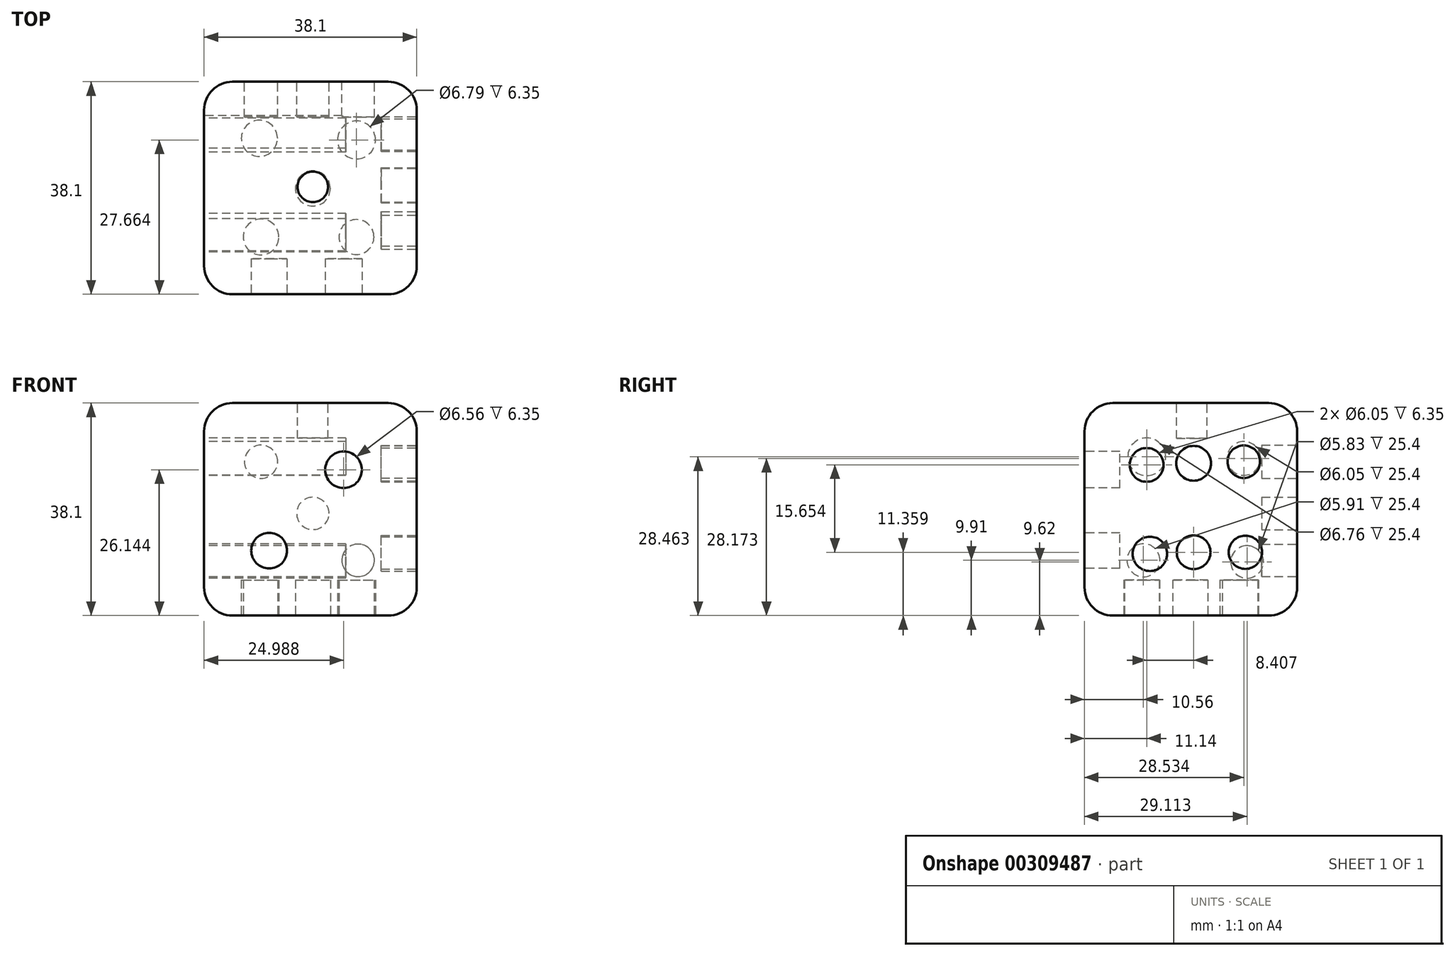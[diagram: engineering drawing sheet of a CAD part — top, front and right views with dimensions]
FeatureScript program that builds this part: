
annotation { "Feature Type Name" : "Feature", "Feature Type Description" : "" }
export const myFeature = defineFeature(function(context is Context, id is Id, definition is map)
    precondition{}
    {
        {
            var Q0;
            Q0=qCreatedBy(makeId("Front.planeOp"),FACE);
            var sketch = newSketch(context, id + "F0", { "sketchPlane" : qUnion([Q0])});
            skLineSegment(sketch, "E0.bottom", {"start": v(-19.48, 2.68) * mm, "end": v(18.62, 2.68) * mm});
            skLineSegment(sketch, "E0.top", {"start": v(-19.48, -35.42) * mm, "end": v(18.62, -35.42) * mm});
            skLineSegment(sketch, "E0.left", {"start": v(-19.48, 2.68) * mm, "end": v(-19.48, -35.42) * mm});
            skLineSegment(sketch, "E0.right", {"start": v(18.62, 2.68) * mm, "end": v(18.62, -35.42) * mm});
            skSolve(sketch);
        }
        {
            var Q0;
            Q0=makeQuery(id+"F0.imprint","IMPRINT",FACE,{"disambiguationData":[TD([[makeQuery(id+"F0.imprint","IMPRINT",EDGE,{"derivedFrom":sQuery(id+"F0.wireOp",EDGE,"E0.bottom")}),-1.0]])]});
            extrude(context, id + "F1", {"entities" : qUnion([Q0]), "depth" : 38.1 * mm});
        }
        {
            var Q0;
            Q0=makeQuery(id+"F1.opExtrude","SWEPT_EDGE",EDGE,{"disambiguationData":[OSD([sQuery(id+"F0.wireOp",EDGE,"E0.bottom"),sQuery(id+"F0.wireOp",EDGE,"E0.left")])]});
            var Q1;
            Q1=makeQuery(id+"F1.opExtrude","CAP_EDGE",EDGE,{"disambiguationData":[OSD([sQuery(id+"F0.wireOp",EDGE,"E0.bottom")])],"isStart":false});
            var Q2;
            Q2=makeQuery(id+"F1.opExtrude","SWEPT_EDGE",EDGE,{"disambiguationData":[OSD([sQuery(id+"F0.wireOp",EDGE,"E0.bottom"),sQuery(id+"F0.wireOp",EDGE,"E0.right")])]});
            var Q3;
            Q3=makeQuery(id+"F1.opExtrude","CAP_EDGE",EDGE,{"disambiguationData":[OSD([sQuery(id+"F0.wireOp",EDGE,"E0.bottom")])],"isStart":true});
            var Q4;
            Q4=makeQuery(id+"F1.opExtrude","CAP_EDGE",EDGE,{"disambiguationData":[OSD([sQuery(id+"F0.wireOp",EDGE,"E0.right")])],"isStart":true});
            var Q5;
            Q5=makeQuery(id+"F1.opExtrude","SWEPT_EDGE",EDGE,{"disambiguationData":[OSD([sQuery(id+"F0.wireOp",EDGE,"E0.top"),sQuery(id+"F0.wireOp",EDGE,"E0.right")])]});
            var Q6;
            Q6=makeQuery(id+"F1.opExtrude","CAP_EDGE",EDGE,{"disambiguationData":[OSD([sQuery(id+"F0.wireOp",EDGE,"E0.top")])],"isStart":true});
            var Q7;
            Q7=makeQuery(id+"F1.opExtrude","CAP_EDGE",EDGE,{"disambiguationData":[OSD([sQuery(id+"F0.wireOp",EDGE,"E0.right")])],"isStart":false});
            var Q8;
            Q8=makeQuery(id+"F1.opExtrude","CAP_EDGE",EDGE,{"disambiguationData":[OSD([sQuery(id+"F0.wireOp",EDGE,"E0.left")])],"isStart":false});
            var Q9;
            Q9=makeQuery(id+"F1.opExtrude","CAP_EDGE",EDGE,{"disambiguationData":[OSD([sQuery(id+"F0.wireOp",EDGE,"E0.top")])],"isStart":false});
            var Q10;
            Q10=makeQuery(id+"F1.opExtrude","SWEPT_EDGE",EDGE,{"disambiguationData":[OSD([sQuery(id+"F0.wireOp",EDGE,"E0.top"),sQuery(id+"F0.wireOp",EDGE,"E0.left")])]});
            var Q11;
            Q11=makeQuery(id+"F1.opExtrude","SWEPT_FACE",FACE,{"disambiguationData":[OSD([sQuery(id+"F0.wireOp",EDGE,"E0.left")])]});
            fillet(context, id + "F2", {"entities" : qUnion([Q0, Q1, Q2, Q3, Q4, Q5, Q6, Q7, Q8, Q9, Q10, Q11]), "radius" : 5.08 * mm, "tangentPropagation" : true, "allowEdgeOverflow" : false});
        }
        {
            var Q0;
            Q0=makeQuery(id+"F1.opExtrude","SWEPT_FACE",FACE,{"disambiguationData":[OSD([sQuery(id+"F0.wireOp",EDGE,"E0.bottom")])]});
            var sketch = newSketch(context, id + "F3", { "sketchPlane" : qUnion([Q0])});
            skCircle(sketch, "E1", {"center": v(0, -18.84) * mm, "radius": 2.73 * mm});
            skSolve(sketch);
        }
        {
            var Q0;
            Q0 = qSketchRegion(id + "F3", true);
            extrude(context, id + "F4", {"entities" : qUnion([Q0]), "operationType" : NewBodyOperationType.REMOVE, "oppositeDirection" : true, "depth" : 6.35 * mm});
        }
        {
            var Q0;
            Q0=makeQuery(id+"F1.opExtrude","CAP_FACE",FACE,{"disambiguationData":[OSD([sQuery(id+"F0.wireOp",EDGE,"E0.bottom"),sQuery(id+"F0.wireOp",EDGE,"E0.top"),sQuery(id+"F0.wireOp",EDGE,"E0.left"),sQuery(id+"F0.wireOp",EDGE,"E0.right")])],"isStart":false});
            var sketch = newSketch(context, id + "F5", { "sketchPlane" : qUnion([Q0])});
            skCircle(sketch, "E2", {"center": v(-7.83, -23.77) * mm, "radius": 3.2 * mm});
            skCircle(sketch, "E3", {"center": v(5.5, -9.28) * mm, "radius": 3.28 * mm});
            skSolve(sketch);
        }
        {
            var Q0;
            Q0 = qSketchRegion(id + "F5", true);
            extrude(context, id + "F6", {"entities" : qUnion([Q0]), "operationType" : NewBodyOperationType.REMOVE, "oppositeDirection" : true, "depth" : 6.35 * mm});
        }
        {
            var Q0;
            Q0=makeQuery(id+"F1.opExtrude","SWEPT_FACE",FACE,{"disambiguationData":[OSD([sQuery(id+"F0.wireOp",EDGE,"E0.top")])]});
            var sketch = newSketch(context, id + "F7", { "sketchPlane" : qUnion([Q0])});
            skCircle(sketch, "E4", {"center": v(0, 19.13) * mm, "radius": 3.14 * mm});
            skCircle(sketch, "E5", {"center": v(7.83, 27.83) * mm, "radius": 3.12 * mm});
            skCircle(sketch, "E6", {"center": v(-9.28, 27.83) * mm, "radius": 3.2 * mm});
            skCircle(sketch, "E7", {"center": v(-9.57, 10.15) * mm, "radius": 3.24 * mm});
            skCircle(sketch, "E8", {"center": v(7.83, 10.44) * mm, "radius": 3.4 * mm});
            skSolve(sketch);
        }
        {
            var Q0;
            Q0 = qSketchRegion(id + "F7", true);
            extrude(context, id + "F8", {"entities" : qUnion([Q0]), "operationType" : NewBodyOperationType.REMOVE, "oppositeDirection" : true, "depth" : 6.35 * mm});
        }
        {
            var Q0;
            Q0=makeQuery(id+"F1.opExtrude","CAP_FACE",FACE,{"disambiguationData":[OSD([sQuery(id+"F0.wireOp",EDGE,"E0.bottom"),sQuery(id+"F0.wireOp",EDGE,"E0.top"),sQuery(id+"F0.wireOp",EDGE,"E0.left"),sQuery(id+"F0.wireOp",EDGE,"E0.right")])],"isStart":true});
            var sketch = newSketch(context, id + "F9", { "sketchPlane" : qUnion([Q0])});
            skCircle(sketch, "E9", {"center": v(0, -17.1) * mm, "radius": 2.9 * mm});
            skCircle(sketch, "E10", {"center": v(9.28, -7.83) * mm, "radius": 2.98 * mm});
            skCircle(sketch, "E11", {"center": v(-8.12, -25.51) * mm, "radius": 2.91 * mm});
            skSolve(sketch);
        }
        {
            var Q0;
            Q0 = qSketchRegion(id + "F9", true);
            extrude(context, id + "F10", {"entities" : qUnion([Q0]), "operationType" : NewBodyOperationType.REMOVE, "oppositeDirection" : true, "depth" : 6.35 * mm});
        }
        {
            var Q0;
            Q0=makeQuery(id+"F1.opExtrude","SWEPT_FACE",FACE,{"disambiguationData":[OSD([sQuery(id+"F0.wireOp",EDGE,"E0.left")])]});
            var sketch = newSketch(context, id + "F11", { "sketchPlane" : qUnion([Q0])});
            skCircle(sketch, "E12", {"center": v(9.57, -7.25) * mm, "radius": 3.03 * mm});
            skCircle(sketch, "E13", {"center": v(27.54, -25.51) * mm, "radius": 2.96 * mm});
            skCircle(sketch, "E14", {"center": v(26.96, -6.96) * mm, "radius": 3.38 * mm});
            skCircle(sketch, "E15", {"center": v(8.99, -25.8) * mm, "radius": 2.91 * mm});
            skSolve(sketch);
        }
        {
            var Q0;
            Q0 = qSketchRegion(id + "F11", true);
            extrude(context, id + "F12", {"entities" : qUnion([Q0]), "operationType" : NewBodyOperationType.REMOVE, "oppositeDirection" : true, "depth" : 25.4 * mm});
        }
        {
            var Q0;
            Q0=makeQuery(id+"F1.opExtrude","SWEPT_FACE",FACE,{"disambiguationData":[OSD([sQuery(id+"F0.wireOp",EDGE,"E0.right")])]});
            var sketch = newSketch(context, id + "F13", { "sketchPlane" : qUnion([Q0])});
            skCircle(sketch, "E16", {"center": v(-18.55, -24.06) * mm, "radius": 3.03 * mm});
            skCircle(sketch, "E17", {"center": v(-18.55, -8.12) * mm, "radius": 3.12 * mm});
            skCircle(sketch, "E18", {"center": v(-26.96, -8.4) * mm, "radius": 3.03 * mm});
            skCircle(sketch, "E19", {"center": v(-26.38, -24.35) * mm, "radius": 3.08 * mm});
            skCircle(sketch, "E20", {"center": v(-9.28, -24.06) * mm, "radius": 2.98 * mm});
            skCircle(sketch, "E21", {"center": v(-9.57, -7.83) * mm, "radius": 2.91 * mm});
            skSolve(sketch);
        }
        {
            var Q0;
            Q0 = qSketchRegion(id + "F13", true);
            extrude(context, id + "F14", {"entities" : qUnion([Q0]), "operationType" : NewBodyOperationType.REMOVE, "oppositeDirection" : true, "depth" : 6.35 * mm});
        }
    });
